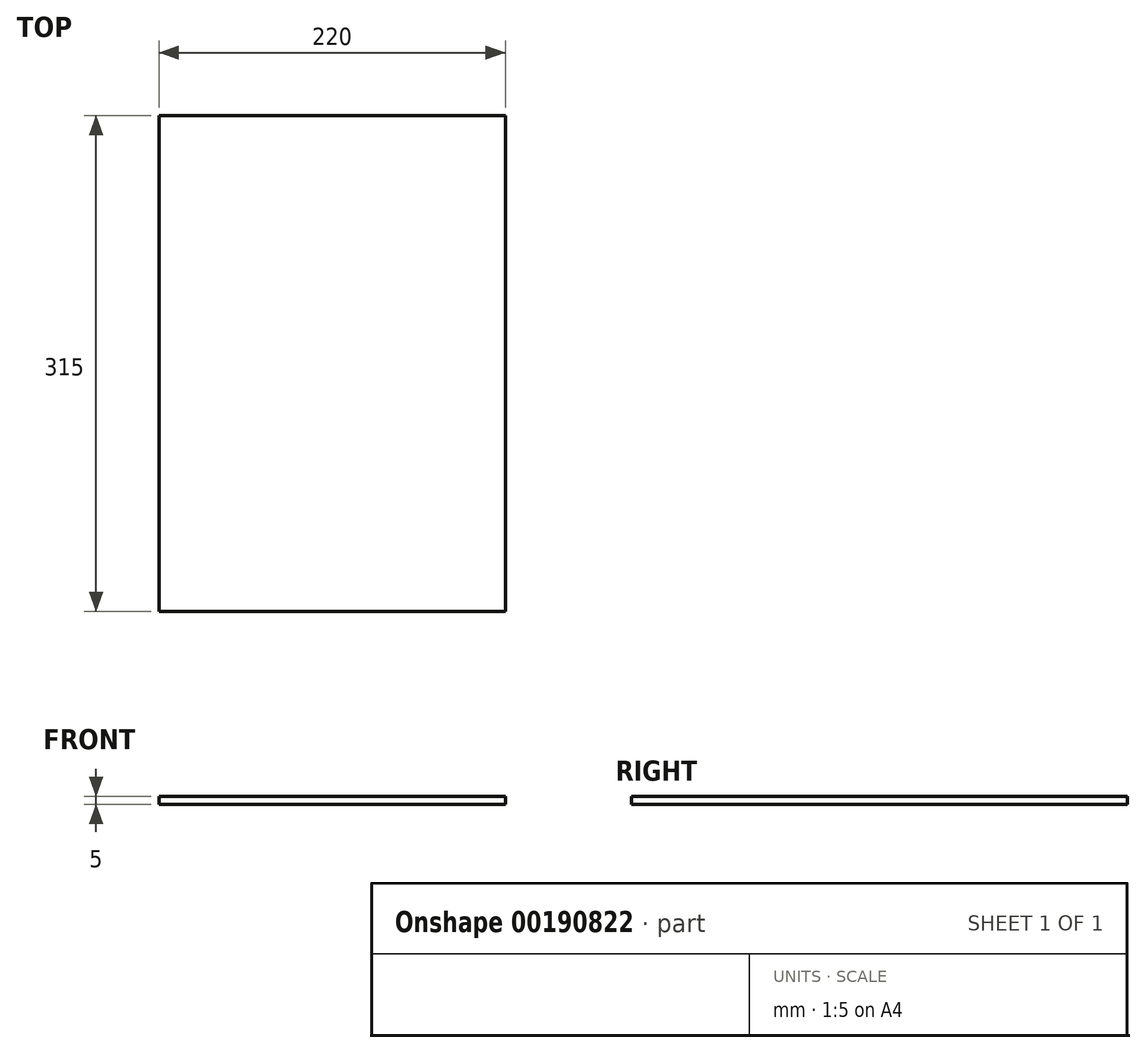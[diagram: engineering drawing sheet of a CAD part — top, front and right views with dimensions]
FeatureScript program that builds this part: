
annotation { "Feature Type Name" : "Feature", "Feature Type Description" : "" }
export const myFeature = defineFeature(function(context is Context, id is Id, definition is map)
    precondition{}
    {
        {
            var Q0;
            Q0=qCreatedBy(makeId("Top.planeOp"),FACE);
            var sketch = newSketch(context, id + "F0", { "sketchPlane" : qUnion([Q0])});
            skLineSegment(sketch, "E0.bottom", {"start": v(110, 157.5) * mm, "end": v(-110, 157.5) * mm});
            skLineSegment(sketch, "E0.top", {"start": v(110, -157.5) * mm, "end": v(-110, -157.5) * mm});
            skLineSegment(sketch, "E0.left", {"start": v(110, 157.5) * mm, "end": v(110, -157.5) * mm});
            skLineSegment(sketch, "E0.right", {"start": v(-110, 157.5) * mm, "end": v(-110, -157.5) * mm});
            skPoint(sketch, "E0.middle", {"position": v(0, 0) * mm});
            skSolve(sketch);
        }
        {
            var Q0;
            Q0 = qSketchRegion(id + "F0", true);
            extrude(context, id + "F1", {"entities" : qUnion([Q0]), "depth" : 5 * mm});
        }
    });
